# Revit family: ГГН-05 КЛ-01
name_source: partatom
category: Устройства вызова и оповещения
revit_build: Autodesk Revit 2017 (Build: 20160225_1515(x64)
units: mm (PartAtom-declared; Revit-internal decimal feet)

## family parameters
Всегда вертикально = Да
Общий = Нет
Основа = Стена
При загрузке вырезать с полостями = Нет
Размер круглого соединителя = Использовать диаметр
Сохранять ориентацию аннотаций = Нет
Тип детали = Нормальный
Точка расчета площади = Нет

## types (1)
- ГГН-05/КЛ-01
    ADSK_Завод-изготовитель = СОУЭ Речор
    ADSK_Масса_Текст = 0.8 кг
    URL = http://rechor.ru
    Высота = 240 мм
    Глубина = 64 мм
    Диапазое рабочих температур = -10 до +50°С
    Изготовитель = СОУЭ Речор
    Исполнение = Настенное
    Код IP = 41
    Материал корпуса = ПВХ
    Наименование = Громкоговоритель ГГН-05/КЛ-01
    Напряжение питания = 100 В
    Описание = Речевой оповещатель. Предназначен для воспроизведения голосовых сообщений, специальных сигналов в системах громкоговорящей связи с высокоомным выходом. Встроенный трансформатор 90..100В. Настенное исполнение.
    Частотный диапазон = 160-16000 Гц
    Ширина = 150 мм
